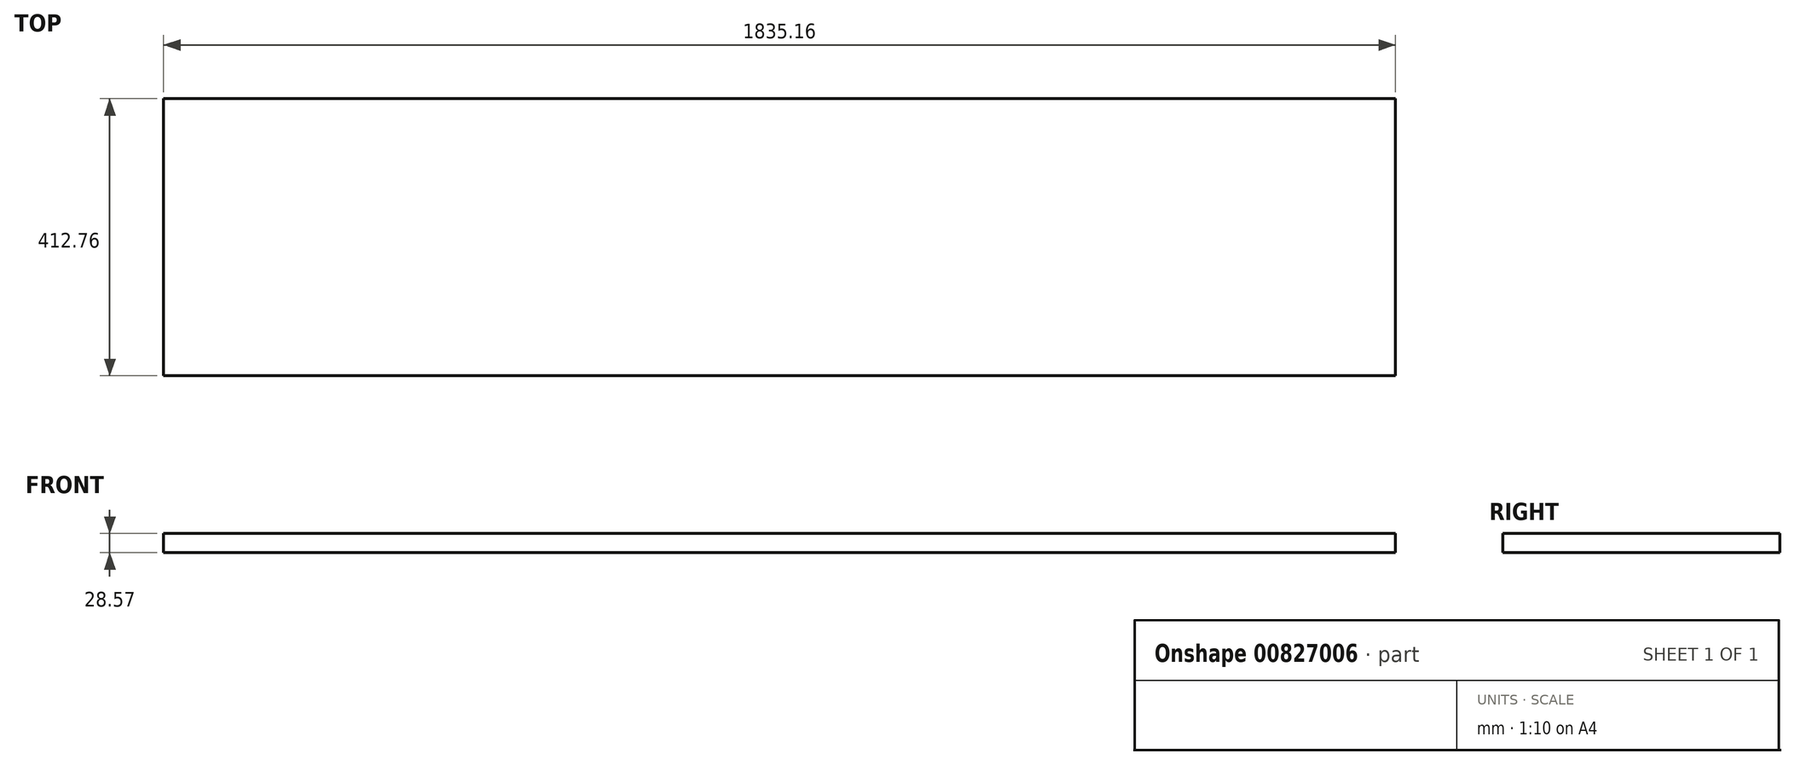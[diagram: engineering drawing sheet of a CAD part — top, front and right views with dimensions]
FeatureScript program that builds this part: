
annotation { "Feature Type Name" : "Feature", "Feature Type Description" : "" }
export const myFeature = defineFeature(function(context is Context, id is Id, definition is map)
    precondition{}
    {
        {
            var Q0;
            Q0=qCreatedBy(makeId("Top.planeOp"),FACE);
            var sketch = newSketch(context, id + "F0", { "sketchPlane" : qUnion([Q0])});
            skLineSegment(sketch, "E0.bottom", {"start": v(917.58, 206.38) * mm, "end": v(-917.58, 206.38) * mm});
            skLineSegment(sketch, "E0.top", {"start": v(917.58, -206.38) * mm, "end": v(-917.58, -206.38) * mm});
            skLineSegment(sketch, "E0.left", {"start": v(917.58, 206.38) * mm, "end": v(917.58, -206.38) * mm});
            skLineSegment(sketch, "E0.right", {"start": v(-917.58, 206.38) * mm, "end": v(-917.58, -206.38) * mm});
            skPoint(sketch, "E0.middle", {"position": v(0, 0) * mm});
            skSolve(sketch);
        }
        {
            var Q0;
            Q0=makeQuery(id+"F0.imprint","IMPRINT",FACE,{"disambiguationData":[TD([[makeQuery(id+"F0.imprint","IMPRINT",EDGE,{"derivedFrom":sQuery(id+"F0.wireOp",EDGE,"E0.bottom")}),1.0]])]});
            extrude(context, id + "F1", {"entities" : qUnion([Q0]), "depth" : 28.57 * mm, "offsetDistance" : 25.4 * mm});
        }
    });
